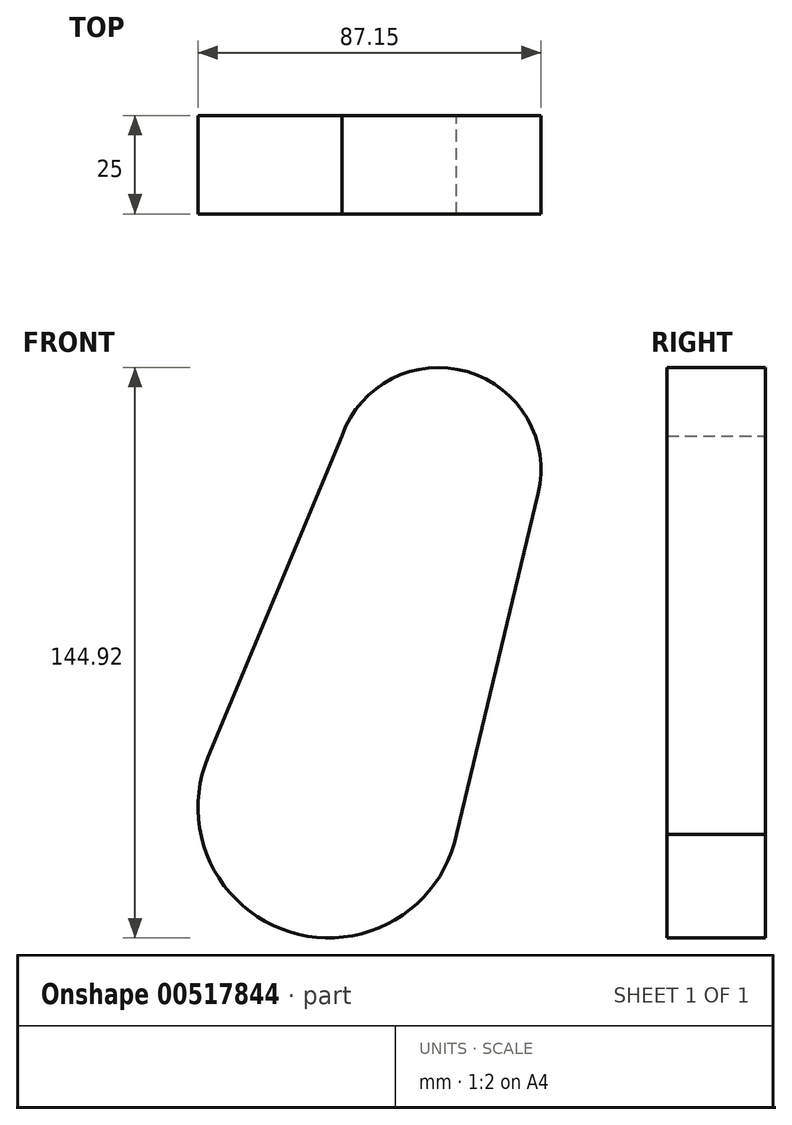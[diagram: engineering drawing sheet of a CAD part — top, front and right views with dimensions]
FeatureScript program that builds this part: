
annotation { "Feature Type Name" : "Feature", "Feature Type Description" : "" }
export const myFeature = defineFeature(function(context is Context, id is Id, definition is map)
    precondition{}
    {
        {
            var Q0;
            Q0=qCreatedBy(makeId("Front.planeOp"),FACE);
            var sketch = newSketch(context, id + "F0", { "sketchPlane" : qUnion([Q0])});
            skCircle(sketch, "E0", {"center": v(0, 65.12) * mm, "radius": 26.06 * mm});
            skCircle(sketch, "E1", {"center": v(-27.88, -20.54) * mm, "radius": 33.21 * mm});
            skLineSegment(sketch, "E2", {"start": v(4.62, -27.4) * mm, "end": v(25.34, 59.04) * mm});
            skLineSegment(sketch, "E3", {"start": v(25.34, 59.04) * mm, "end": v(-23.47, 76.43) * mm});
            skLineSegment(sketch, "E4", {"start": v(-23.47, 76.43) * mm, "end": v(-58.54, -7.77) * mm});
            skLineSegment(sketch, "E5", {"start": v(116.8, 105.17) * mm, "end": v(116.8, 105.17) * mm});
            skSolve(sketch);
        }
        {
            var Q0;
            Q0 = qSketchRegion(id + "F0", true);
            extrude(context, id + "F1", {"entities" : qUnion([Q0]), "depth" : 25 * mm, "offsetDistance" : 25 * mm});
        }
    });
